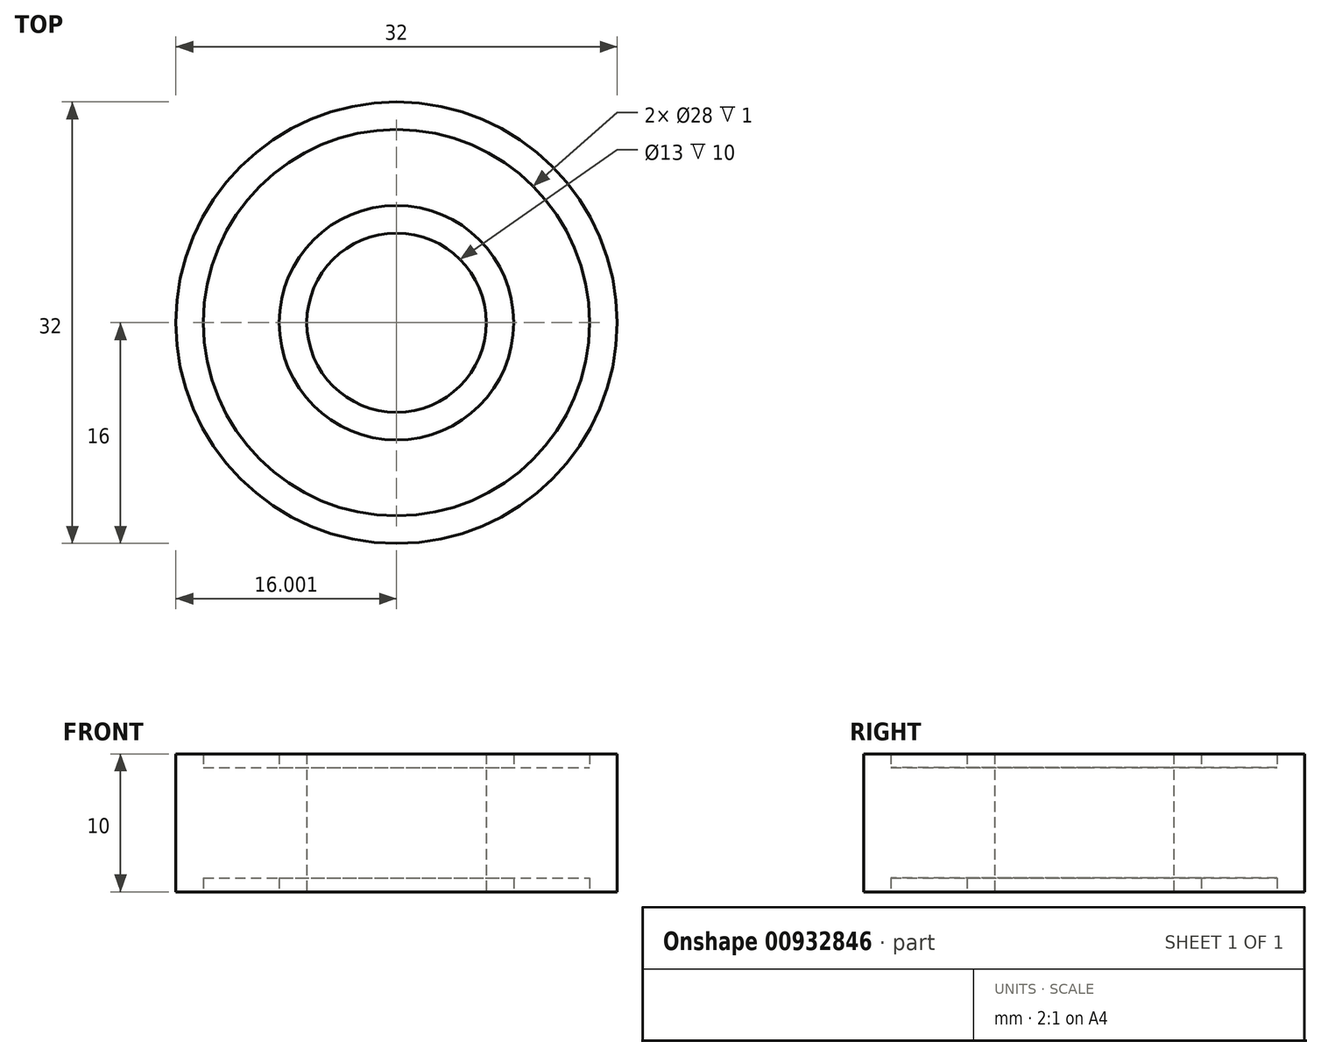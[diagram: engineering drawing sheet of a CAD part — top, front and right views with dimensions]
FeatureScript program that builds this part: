
annotation { "Feature Type Name" : "Feature", "Feature Type Description" : "" }
export const myFeature = defineFeature(function(context is Context, id is Id, definition is map)
    precondition{}
    {
        {
            var Q0;
            Q0=qCreatedBy(makeId("Front.planeOp"),FACE);
            var sketch = newSketch(context, id + "F0", { "sketchPlane" : qUnion([Q0])});
            skLineSegment(sketch, "E0", {"start": v(-46.29, 16.4) * mm, "end": v(-46.29, 26.4) * mm});
            skLineSegment(sketch, "E1", {"start": v(-46.29, 26.4) * mm, "end": v(-44.29, 26.4) * mm});
            skLineSegment(sketch, "E2", {"start": v(-44.29, 26.4) * mm, "end": v(-44.29, 25.4) * mm});
            skLineSegment(sketch, "E3", {"start": v(-46.29, 16.4) * mm, "end": v(-44.29, 16.4) * mm});
            skLineSegment(sketch, "E4", {"start": v(-44.29, 16.4) * mm, "end": v(-44.29, 17.4) * mm});
            skLineSegment(sketch, "E5", {"start": v(-44.29, 17.4) * mm, "end": v(-38.79, 17.4) * mm});
            skLineSegment(sketch, "E6", {"start": v(-38.79, 17.4) * mm, "end": v(-38.79, 16.4) * mm});
            skLineSegment(sketch, "E7", {"start": v(-38.79, 16.4) * mm, "end": v(-36.79, 16.4) * mm});
            skLineSegment(sketch, "E8", {"start": v(-36.79, 16.4) * mm, "end": v(-36.79, 26.4) * mm});
            skLineSegment(sketch, "E9", {"start": v(-36.79, 26.4) * mm, "end": v(-38.79, 26.4) * mm});
            skLineSegment(sketch, "E10", {"start": v(-38.79, 26.4) * mm, "end": v(-38.79, 25.4) * mm});
            skLineSegment(sketch, "E11", {"start": v(-38.79, 25.4) * mm, "end": v(-44.29, 25.4) * mm});
            skLineSegment(sketch, "E12", {"start": v(-46.29, 21.4) * mm, "end": v(-30.29, 21.4) * mm, "construction": true});
            skLineSegment(sketch, "E13", {"start": v(-30.29, 16.49) * mm, "end": v(-30.29, 26.06) * mm, "construction": true});
            skSolve(sketch);
        }
        {
            var Q0;
            Q0=makeQuery(id+"F0.imprint","IMPRINT",FACE,{"disambiguationData":[TD([[makeQuery(id+"F0.imprint","IMPRINT",EDGE,{"derivedFrom":sQuery(id+"F0.wireOp",EDGE,"E0")}),-1.0]])]});
            var Q1;
            Q1=sQuery(id+"F0.wireOp",EDGE,"E13");
            revolve(context, id + "F1", {"surfaceOperationType" : NewSurfaceOperationType.NEW, "entities" : qUnion([Q0]), "axis" : qUnion([Q1]), "revolveType" : RevolveType.FULL});
        }
    });
